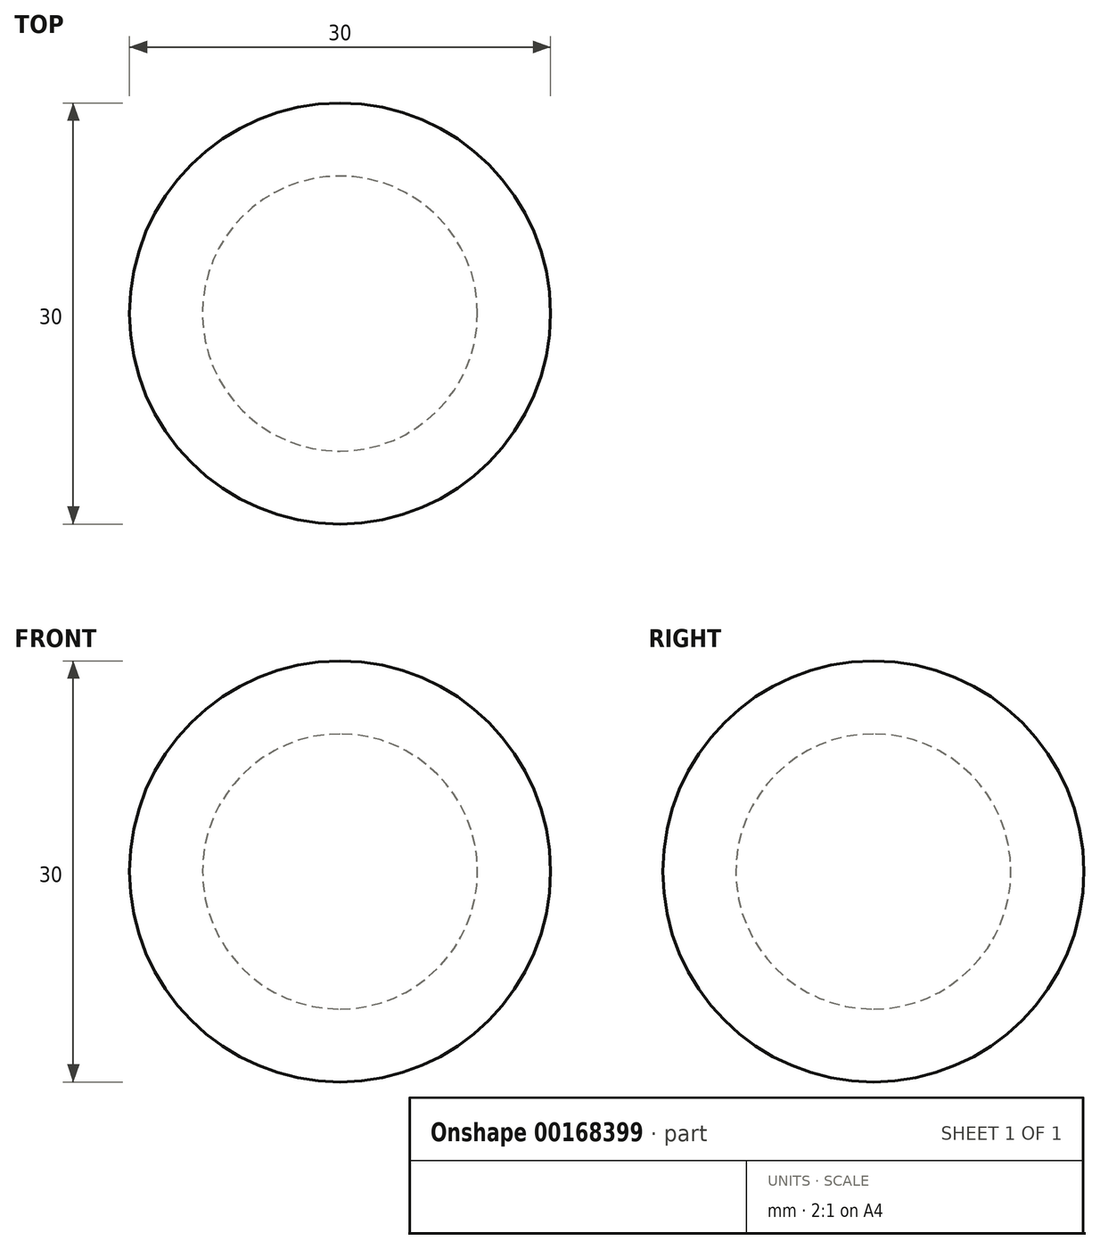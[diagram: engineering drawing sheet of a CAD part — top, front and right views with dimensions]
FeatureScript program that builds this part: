
annotation { "Feature Type Name" : "Feature", "Feature Type Description" : "" }
export const myFeature = defineFeature(function(context is Context, id is Id, definition is map)
    precondition{}
    {
        {
            var Q0;
            Q0=qCreatedBy(makeId("Front.planeOp"),FACE);
            var sketch = newSketch(context, id + "F0", { "sketchPlane" : qUnion([Q0]), "disableImprinting" : false});
            skArc(sketch, "E0", {"start": v(0, 9.8) * mm, "mid": v(-9.8, 0) * mm, "end": v(0, -9.8) * mm});
            skArc(sketch, "E1", {"start": v(0, 15) * mm, "mid": v(-15, 0) * mm, "end": v(0, -15) * mm});
            skLineSegment(sketch, "E2", {"start": v(0, 15) * mm, "end": v(0, 9.8) * mm});
            skLineSegment(sketch, "E3", {"start": v(0, 21.29) * mm, "end": v(0, -17.46) * mm, "construction": true});
            skLineSegment(sketch, "E4", {"start": v(0, -15) * mm, "end": v(0, -9.8) * mm});
            skSolve(sketch);
        }
        {
            var Q0;
            Q0=makeQuery(id+"F0.imprint","IMPRINT",FACE,{"disambiguationData":[TD([[makeQuery(id+"F0.imprint","IMPRINT",EDGE,{"derivedFrom":sQuery(id+"F0.wireOp",EDGE,"E0")}),-1.0]])]});
            var Q1;
            Q1=sQuery(id+"F0.wireOp",EDGE,"E3");
            revolve(context, id + "F1", {"entities" : qUnion([Q0]), "axis" : qUnion([Q1]), "revolveType" : RevolveType.FULL});
        }
    });
